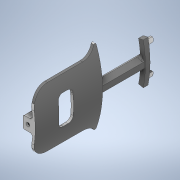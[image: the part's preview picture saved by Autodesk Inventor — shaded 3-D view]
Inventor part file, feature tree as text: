
AUTODESK INVENTOR PART (.ipt)
format: ipt  version: 2020 (Build 240168000, 168)  size: 704,512 bytes
history: native  units: mm
features: projected_geometry x39, extrude x19, sketch x18, fillet x12, plane x1
ambient origin geometry x8: Origin, YZ Plane, XZ Plane, XY Plane, X Axis, Y Axis, Z Axis, Center Point
bodies: Solid1 (feature_tree)
feature tree (89):
  extrude  "Extrusion1"  Depth=88.0mm
  fillet  "Fillet1"  Radius=5.61996mm
  extrude  "Extrusion2"  Depth=2.80998mm
  fillet  "Fillet2"  Radius=5.61996mm
  fillet  "Fillet3"  Radius=90.0mm
  extrude  "Extrusion3"  Depth=84.0mm
  fillet  "Fillet4"  Radius=29.670597mm
  plane  "Work Plane1"
  extrude  "Extrusion4"  Depth=29.670597mm
  extrude  "Extrusion5"  Depth=7.95mm TaperAngle=0.0deg
  extrude  "Extrusion6"  Depth=4.0mm
  fillet  "Fillet5"  Radius=2.0mm
  extrude  "Extrusion7"  Depth=2.443461mm
  extrude  "Extrusion8"  Depth=1.0mm
  extrude  "Extrusion9"  TaperAngle=0.0deg  [1 undecoded]
  extrude  "Extrusion10"  Depth=8.2mm
  sketch  "Sketch12"  dims[d34=46.4mm d35=0.0mm d36=1.6mm d37=0.0mm d38=2.0mm]
  extrude  "Extrusion11"  Depth=1.6mm TaperAngle=0.0deg
  fillet  "Fillet9"  Radius=2.0mm
  extrude  "Extrusion12"  Depth=8.0mm TaperAngle=0.0deg
  extrude  "Extrusion13"  Depth=26.87807mm
  extrude  "Extrusion14"  Depth=88.0mm
  fillet  "Fillet10"  Radius=88.0mm
  extrude  "Extrusion15"  Depth=88.0mm
  extrude  "Extrusion16"  Depth=15.0mm TaperAngle=0.0deg
  fillet  "Fillet11"  Radius=81.45mm
  fillet  "Fillet12"  Radius=15.0mm
  fillet  "Fillet13"  Radius=29.452431mm
  extrude  "Extrusion17"  Depth=0.9mm TaperAngle=0.0deg
  fillet  "Fillet14"  Radius=28.0mm
  extrude  "Extrusion18"  Depth=10.0mm
  extrude  "Extrusion19"  Depth=10.0mm
  fillet  "Fillet15"  Radius=38.65mm
  sketch  "Sketch1"  dims[d0=88.0mm d1=2.80998mm d2=5.61996mm]
  sketch  "Sketch2"  dims[d3=86.0mm d4=2.80998mm d5=5.61996mm d6=90.0mm d7=0.0mm]
  projected_geometry  "Projected Loop1"
  sketch  "Sketch3"  dims[d8=14.0mm d9=84.0mm d10=29.670597mm]
  projected_geometry  "Projected Loop2"
  sketch  "Sketch5"  dims[d11=3.490659mm d12=29.670597mm]
  projected_geometry  "Projected Loop4"
  projected_geometry  "Projected Loop5"
  projected_geometry  "Projected Loop6"
  projected_geometry  "Projected Loop7"
  sketch  "Sketch6"  dims[d13=29.670597mm d14=7.95mm d15=16.0mm d16=0.0mm d17=0.0mm]
  projected_geometry  "Projected Loop8"
  sketch  "Sketch7"  dims[d18=14.0mm d19=4.0mm d20=2.0mm]
  projected_geometry  "Projected Loop9"
  projected_geometry  "Projected Loop10"
  projected_geometry  "Projected Loop11"
  projected_geometry  "Projected Loop12"
  projected_geometry  "Projected Loop13"
  projected_geometry  "Projected Loop14"
  projected_geometry  "Projected Loop15"
  projected_geometry  "Projected Loop16"
  projected_geometry  "Projected Loop17"
  sketch  "Sketch8"  dims[d21=30.194196mm d22=2.443461mm]
  projected_geometry  "Projected Loop18"
  sketch  "Sketch9"  dims[d23=4.2mm d24=0.0mm d25=1.0mm]
  projected_geometry  "Projected Loop19"
  projected_geometry  "Projected Loop20"
  projected_geometry  "Projected Loop21"
  sketch  "Sketch10"  dims[d29=10.0mm d30=0.0mm d31=0.0mm]
  projected_geometry  "Projected Loop22"
  sketch  "Sketch11"  dims[d32=83.5mm d33=8.2mm]
  projected_geometry  "Projected Loop23"
  projected_geometry  "Projected Loop24"
  projected_geometry  "Projected Loop25"
  projected_geometry  "Projected Loop26"
  sketch  "Sketch13"  dims[d39=6.0mm d40=0.0mm d43=8.0mm d44=0.0mm]
  projected_geometry  "Projected Loop27"
  sketch  "Sketch14"  dims[d45=86.0mm d46=26.87807mm]
  sketch  "Sketch15"  dims[d47=86.0mm d48=26.87807mm d49=88.0mm]
  projected_geometry  "Projected Loop28"
  sketch  "Sketch16"  dims[d50=26.87807mm d51=88.0mm]
  sketch  "Sketch17"  dims[d52=26.87807mm d53=15.0mm d54=0.0mm d56=81.45mm d57=15.0mm d58=0.0mm d59=29.452431mm]
  projected_geometry  "Projected Loop29"
  projected_geometry  "Projected Loop30"
  projected_geometry  "Projected Loop31"
  projected_geometry  "Projected Loop32"
  projected_geometry  "Projected Loop33"
  projected_geometry  "Projected Loop34"
  projected_geometry  "Projected Loop35"
  projected_geometry  "Projected Loop36"
  projected_geometry  "Projected Loop37"
  sketch  "Sketch18"  dims[d60=29.452431mm d61=0.9mm d62=0.0mm d63=28.0mm]
  sketch  "Sketch19"  dims[d64=28.0mm d65=13.2mm d66=13.2mm d67=38.65mm d68=38.65mm d69=27.85mm d70=27.85mm d71=29.0mm d72=29.0mm d73=28.0mm d74=28.0mm d75=100.0mm d76=0.0mm d77=0.0mm d78=1.0mm d79=3.0mm d80=0.0mm d81=3.0mm d82=0.0mm d83=86.917mm d84=0.0mm d85=3.0mm d86=0.0mm d87=82.0mm d88=8.0mm d89=10.0mm d90=10.0mm d91=0.0mm d92=2.0mm d93=2.6mm d94=5.6mm d95=2.8mm d96=1.3mm d97=5.6mm d98=0.0mm d99=60.0deg d100=60.0deg d101=6.0mm d102=0.0mm d103=2.0mm d104=1.0mm d105=2.0mm d106=12.0mm d107=22.0mm d108=24.0mm d109=2.755305mm d110=12.0mm d111=4.0mm d112=85.8mm d113=29.757864mm d114=3.316126mm d115=84.2mm d116=3.316126mm d117=10.0mm d118=0.0mm d119=0.5mm d120=5.2mm d121=1.9mm d122=0.0mm d123=0.2mm d124=0.0mm d125=10.0mm d126=0.872665mm]
  projected_geometry  "Projected Loop38"
  projected_geometry  "Projected Loop39"
  projected_geometry  "Projected Loop40"
note: 1 required parameter value undecoded (feature->parameter linkage not recoverable at this tier; creation-order binding heuristic only, values carry confidence <= 0.55)
